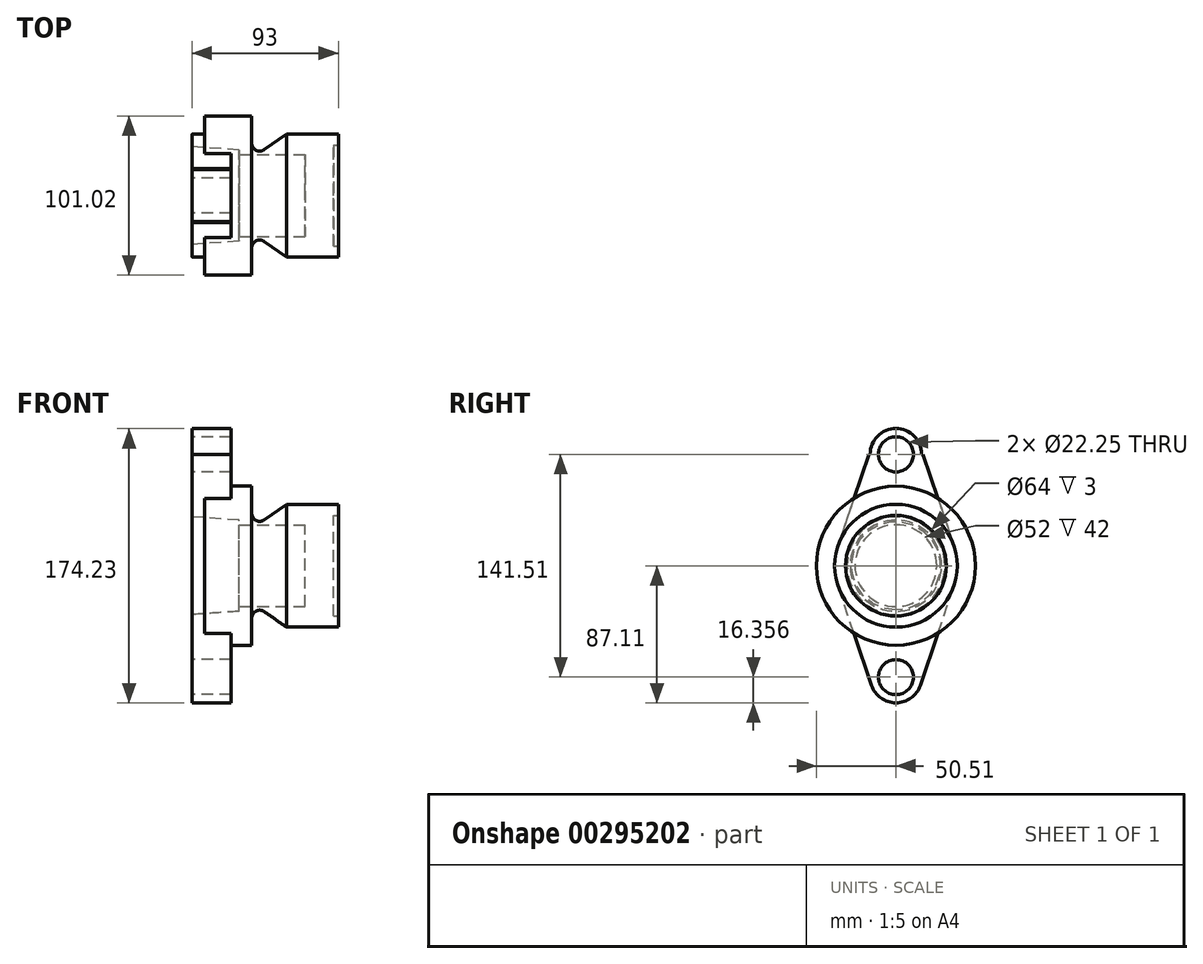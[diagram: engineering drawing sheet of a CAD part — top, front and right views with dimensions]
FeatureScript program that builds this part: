
annotation { "Feature Type Name" : "Feature", "Feature Type Description" : "" }
export const myFeature = defineFeature(function(context is Context, id is Id, definition is map)
    precondition{}
    {
        {
            var Q0;
            Q0=qCreatedBy(makeId("Front.planeOp"),FACE);
            var sketch = newSketch(context, id + "F0", { "sketchPlane" : qUnion([Q0])});
            skLineSegment(sketch, "E0", {"start": v(0, 77.18) * mm, "end": v(8, 77.18) * mm});
            skLineSegment(sketch, "E1", {"start": v(8, 88.69) * mm, "end": v(8, 77.18) * mm});
            skLineSegment(sketch, "E2", {"start": v(8, 88.69) * mm, "end": v(38, 88.69) * mm});
            skLineSegment(sketch, "E3", {"start": v(38, 88.69) * mm, "end": v(38, 71.38) * mm});
            skLineSegment(sketch, "E4", {"start": v(93, 77.18) * mm, "end": v(93, 70.18) * mm});
            skLineSegment(sketch, "E5", {"start": v(93, 70.18) * mm, "end": v(90, 70.18) * mm});
            skLineSegment(sketch, "E6", {"start": v(90, 70.18) * mm, "end": v(90, 38.18) * mm});
            skLineSegment(sketch, "E7", {"start": v(90, 38.18) * mm, "end": v(72, 38.18) * mm});
            skLineSegment(sketch, "E8", {"start": v(72, 38.18) * mm, "end": v(72, 64.18) * mm});
            skLineSegment(sketch, "E9", {"start": v(72, 64.18) * mm, "end": v(30, 64.18) * mm});
            skLineSegment(sketch, "E10", {"start": v(0, 69.18) * mm, "end": v(0, 77.18) * mm});
            skLineSegment(sketch, "E11", {"start": v(30, 64.18) * mm, "end": v(30, 67.18) * mm});
            skLineSegment(sketch, "E12", {"start": v(30, 67.18) * mm, "end": v(0, 69.18) * mm});
            skLineSegment(sketch, "E13", {"start": v(45.87, 67.28) * mm, "end": v(60, 77.18) * mm});
            skLineSegment(sketch, "E14", {"start": v(60, 77.18) * mm, "end": v(93, 77.18) * mm});
            skPoint(sketch, "E15.visualSharp", {"position": v(38, 61.78) * mm});
            skArc(sketch, "E15.filletArc", {"start": v(38, 71.38) * mm, "mid": v(40.7, 66.95) * mm, "end": v(45.87, 67.28) * mm});
            skSolve(sketch);
        }
        {
            var Q0;
            Q0=makeQuery(id+"F0.imprint","IMPRINT",FACE,{"disambiguationData":[TD([[makeQuery(id+"F0.imprint","IMPRINT",EDGE,{"derivedFrom":sQuery(id+"F0.wireOp",EDGE,"E0")}),-1.0]])]});
            var Q1;
            Q1=sQuery(id+"F0.wireOp",EDGE,"E7");
            revolve(context, id + "F1", {"entities" : qUnion([Q0]), "axis" : qUnion([Q1]), "revolveType" : RevolveType.FULL});
        }
        {
            var Q0;
            Q0=qCreatedBy(makeId("Right.planeOp"),FACE);
            var sketch = newSketch(context, id + "F2", { "sketchPlane" : qUnion([Q0])});
            skLineSegment(sketch, "E16", {"start": v(0, 0) * mm, "end": v(0, 108.94) * mm});
            skCircle(sketch, "E17", {"center": v(0, 108.94) * mm, "radius": 11.12 * mm});
            skArc(sketch, "E18", {"start": v(16.36, 108.94) * mm, "mid": v(0, 125.3) * mm, "end": v(-16.36, 108.94) * mm});
            skLineSegment(sketch, "E19", {"start": v(16.36, 108.94) * mm, "end": v(17.27, 108.94) * mm});
            skLineSegment(sketch, "E20", {"start": v(17.27, 108.94) * mm, "end": v(16.36, 108.94) * mm});
            skPoint(sketch, "E21.endSnap0", {"position": v(56.98, 38.18) * mm});
            skPoint(sketch, "E22.orphan", {"position": v(113.96, 38.18) * mm});
            skPoint(sketch, "E23.trimOffspring.end.orphan", {"position": v(-96.3, 38.18) * mm});
            skPoint(sketch, "E23.trimOffspring.start.orphan", {"position": v(0, 38.18) * mm});
            skCircle(sketch, "E24", {"center": v(0, 38.18) * mm, "radius": 39 * mm});
            skLineSegment(sketch, "E25", {"start": v(-15.5, 114.17) * mm, "end": v(-36.95, 50.66) * mm});
            skLineSegment(sketch, "E26", {"start": v(15.5, 114.17) * mm, "end": v(36.95, 50.66) * mm});
            skLineSegment(sketch, "E27.trimOffspring", {"start": v(-16.36, 108.94) * mm, "end": v(-17.27, 108.94) * mm});
            skLineSegment(sketch, "E28", {"start": v(56.98, 38.18) * mm, "end": v(-96.3, 38.18) * mm});
            skLineSegment(sketch, "E29.MirrorCS", {"start": v(15.5, -37.8) * mm, "end": v(36.95, 25.7) * mm});
            skArc(sketch, "E30.MirrorCS", {"start": v(16.36, -32.57) * mm, "mid": v(0, -48.93) * mm, "end": v(-16.36, -32.57) * mm});
            skLineSegment(sketch, "E31.MirrorCS", {"start": v(-15.5, -37.8) * mm, "end": v(-36.95, 25.7) * mm});
            skCircle(sketch, "E32.MirrorC", {"center": v(0, -32.57) * mm, "radius": 11.12 * mm});
            skSolve(sketch);
        }
        {
            var Q0;
            Q0=makeQuery(id+"F2.imprint","IMPRINT",FACE,{"disambiguationData":[TD([[makeQuery(id+"F2.imprint","IMPRINT",EDGE,{"derivedFrom":sQuery(id+"F2.wireOp",EDGE,"E17")}),-1.0]])]});
            var Q1;
            {var subQ1=sQuery(id+"F2.wireOp",EDGE,"E29.MirrorCS");Q1=makeQuery(id+"F2.imprint","IMPRINT",FACE,{"disambiguationData":[TD([[makeQuery(id+"F2.imprint","IMPRINT",EDGE,{"derivedFrom":subQ1}),1.0]])]});}
            extrude(context, id + "F3", {"entities" : qUnion([Q0, Q1]), "operationType" : NewBodyOperationType.ADD, "depth" : 25 * mm});
        }
    });
